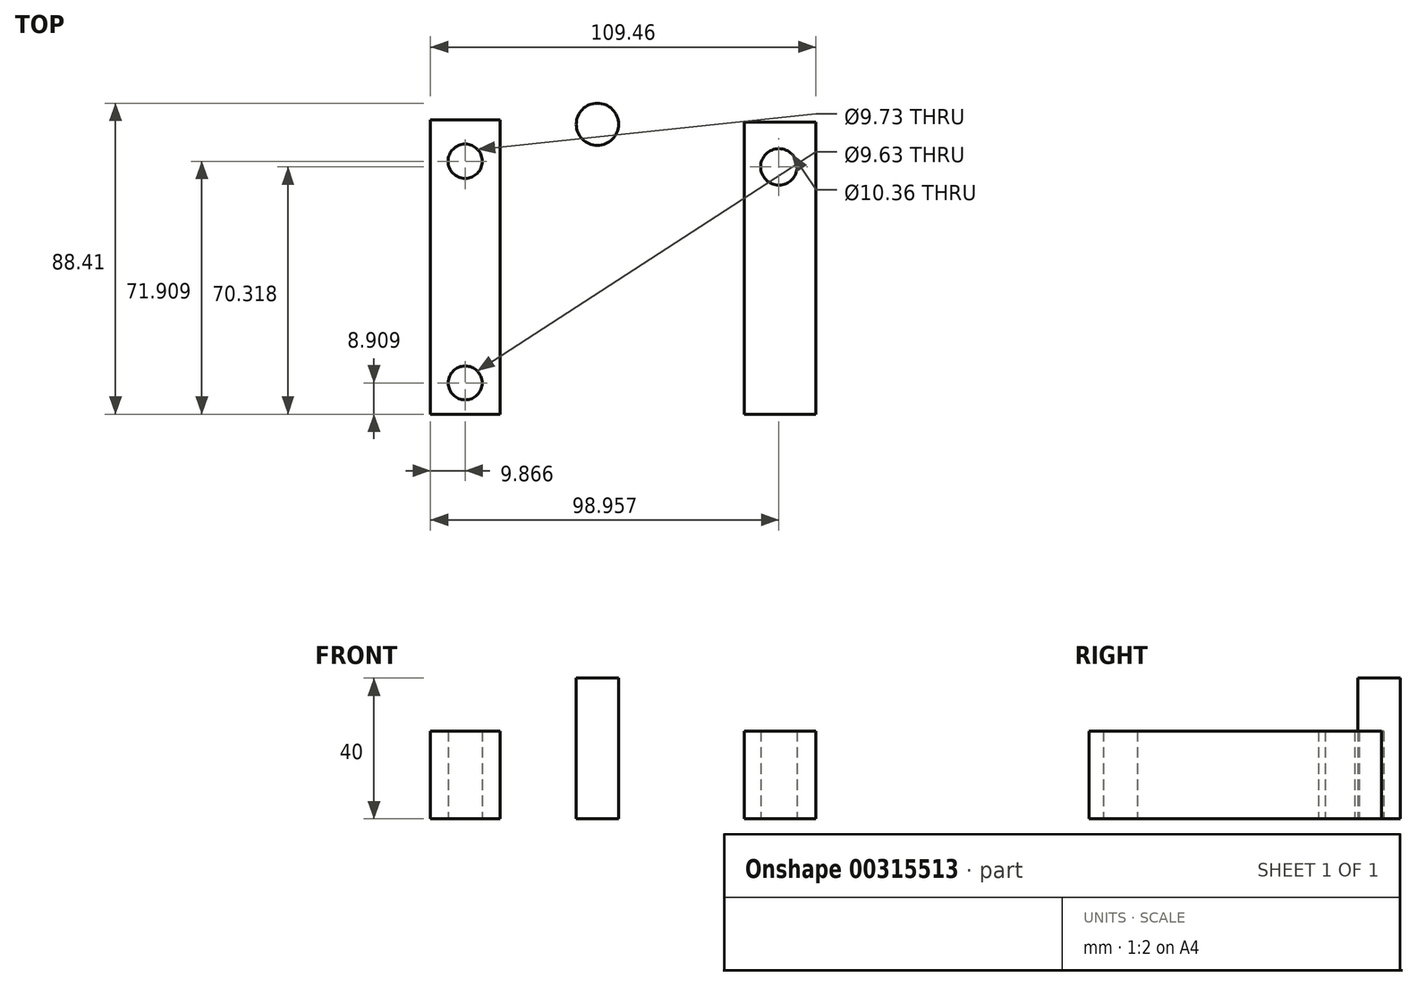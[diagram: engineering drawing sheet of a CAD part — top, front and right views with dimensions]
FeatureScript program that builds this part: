
annotation { "Feature Type Name" : "Feature", "Feature Type Description" : "" }
export const myFeature = defineFeature(function(context is Context, id is Id, definition is map)
    precondition{}
    {
        {
            var Q0;
            Q0=qCreatedBy(makeId("Top.planeOp"),FACE);
            var sketch = newSketch(context, id + "F0", { "sketchPlane" : qUnion([Q0])});
            skLineSegment(sketch, "E0.bottom", {"start": v(-38.5, 50.11) * mm, "end": v(-58.23, 50.11) * mm});
            skLineSegment(sketch, "E0.top", {"start": v(-38.5, -33.57) * mm, "end": v(-58.23, -33.57) * mm});
            skLineSegment(sketch, "E0.left", {"start": v(-38.5, 50.11) * mm, "end": v(-38.5, -33.57) * mm});
            skLineSegment(sketch, "E0.right", {"start": v(-58.23, 50.11) * mm, "end": v(-58.23, -33.57) * mm});
            skLineSegment(sketch, "E1.bottom", {"start": v(30.86, 49.48) * mm, "end": v(51.23, 49.48) * mm});
            skLineSegment(sketch, "E1.top", {"start": v(30.86, -33.57) * mm, "end": v(51.23, -33.57) * mm});
            skLineSegment(sketch, "E1.left", {"start": v(30.86, 49.48) * mm, "end": v(30.86, -33.57) * mm});
            skLineSegment(sketch, "E1.right", {"start": v(51.23, 49.48) * mm, "end": v(51.23, -33.57) * mm});
            skCircle(sketch, "E2", {"center": v(-48.36, 38.34) * mm, "radius": 4.87 * mm});
            skCircle(sketch, "E3", {"center": v(-48.36, -24.66) * mm, "radius": 4.81 * mm});
            skCircle(sketch, "E4", {"center": v(40.73, 36.75) * mm, "radius": 5.18 * mm});
            skSolve(sketch);
        }
        {
            var Q0;
            Q0=qCreatedBy(makeId("Top.planeOp"),FACE);
            var sketch = newSketch(context, id + "F1", { "sketchPlane" : qUnion([Q0])});
            skCircle(sketch, "E5", {"center": v(-48.36, 42.48) * mm, "radius": 6 * mm});
            skCircle(sketch, "E6", {"center": v(41.05, 42.48) * mm, "radius": 6 * mm});
            skCircle(sketch, "E7", {"center": v(-10.82, 48.84) * mm, "radius": 6 * mm});
            skSolve(sketch);
        }
        {
            var Q0;
            Q0=makeQuery(id+"F0.imprint","IMPRINT",FACE,{"disambiguationData":[TD([[makeQuery(id+"F0.imprint","IMPRINT",EDGE,{"derivedFrom":sQuery(id+"F0.wireOp",EDGE,"E1.bottom")}),-1.0]])]});
            var Q1;
            Q1=makeQuery(id+"F0.imprint","IMPRINT",FACE,{"disambiguationData":[TD([[makeQuery(id+"F0.imprint","IMPRINT",EDGE,{"derivedFrom":sQuery(id+"F0.wireOp",EDGE,"E0.bottom")}),1.0]])]});
            extrude(context, id + "F2", {"entities" : qUnion([Q0, Q1]), "depth" : 25 * mm});
        }
        {
            var Q0;
            Q0=makeQuery(id+"F1.imprint","IMPRINT",FACE,{"disambiguationData":[TD([[makeQuery(id+"F1.imprint","IMPRINT",EDGE,{"derivedFrom":sQuery(id+"F1.wireOp",EDGE,"E7")}),1.0]])]});
            extrude(context, id + "F3", {"entities" : qUnion([Q0]), "depth" : 40 * mm});
        }
        {
            var Q0;
            Q0=makeQuery(id+"F0.imprint","IMPRINT",FACE,{"disambiguationData":[TD([[makeQuery(id+"F0.imprint","IMPRINT",EDGE,{"derivedFrom":sQuery(id+"F0.wireOp",EDGE,"E2")}),1.0]])]});
            var Q1;
            Q1=makeQuery(id+"F0.imprint","IMPRINT",FACE,{"disambiguationData":[TD([[makeQuery(id+"F0.imprint","IMPRINT",EDGE,{"derivedFrom":sQuery(id+"F0.wireOp",EDGE,"E3")}),1.0]])]});
            var Q2;
            Q2=makeQuery(id+"F0.imprint","IMPRINT",FACE,{"disambiguationData":[TD([[makeQuery(id+"F0.imprint","IMPRINT",EDGE,{"derivedFrom":sQuery(id+"F0.wireOp",EDGE,"E4")}),1.0]])]});
            extrude(context, id + "F4", {"entities" : qUnion([Q0, Q1, Q2]), "operationType" : NewBodyOperationType.REMOVE, "endBound" : BoundingType.SYMMETRIC, "oppositeDirection" : true, "depth" : 50 * mm});
        }
    });
